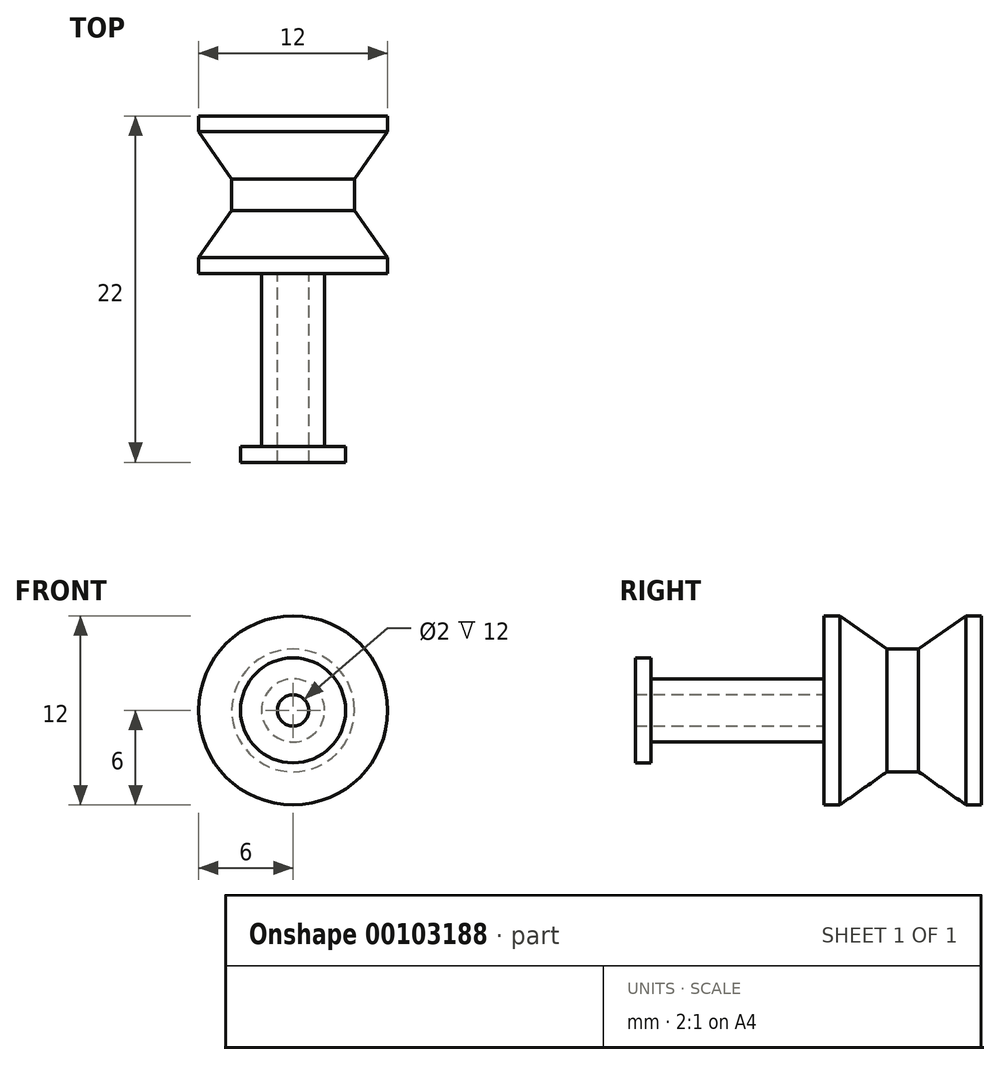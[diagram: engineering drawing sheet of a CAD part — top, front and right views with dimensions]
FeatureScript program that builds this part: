
annotation { "Feature Type Name" : "Feature", "Feature Type Description" : "" }
export const myFeature = defineFeature(function(context is Context, id is Id, definition is map)
    precondition{}
    {
        {
            var Q0;
            Q0=qCreatedBy(makeId("Front.planeOp"),FACE);
            var sketch = newSketch(context, id + "F0", { "sketchPlane" : qUnion([Q0])});
            skCircle(sketch, "E0", {"center": v(0, 0) * mm, "radius": 1 * mm});
            skCircle(sketch, "E1", {"center": v(0, 0) * mm, "radius": 2 * mm});
            skCircle(sketch, "E2", {"center": v(0, 0) * mm, "radius": 3.5 * mm});
            skCircle(sketch, "E3", {"center": v(0, 0) * mm, "radius": 6 * mm});
            skSolve(sketch);
        }
        {
            var Q0;
            Q0=makeQuery(id+"F0.imprint","IMPRINT",FACE,{"disambiguationData":[TD([[makeQuery(id+"F0.imprint","IMPRINT",EDGE,{"derivedFrom":sQuery(id+"F0.wireOp",EDGE,"E0")}),-1.0]])]});
            extrude(context, id + "F1", {"entities" : qUnion([Q0]), "depth" : 22 * mm});
        }
        {
            var Q0;
            Q0=makeQuery(id+"F0.imprint","IMPRINT",FACE,{"disambiguationData":[TD([[makeQuery(id+"F0.imprint","IMPRINT",EDGE,{"derivedFrom":sQuery(id+"F0.wireOp",EDGE,"E2")}),-1.0]])]});
            var Q1;
            Q1=makeQuery(id+"F0.imprint","IMPRINT",FACE,{"disambiguationData":[TD([[makeQuery(id+"F0.imprint","IMPRINT",EDGE,{"derivedFrom":sQuery(id+"F0.wireOp",EDGE,"E1")}),-1.0]])]});
            var Q2;
            Q2=makeQuery(id+"F0.imprint","IMPRINT",FACE,{"disambiguationData":[TD([[makeQuery(id+"F0.imprint","IMPRINT",EDGE,{"derivedFrom":sQuery(id+"F0.wireOp",EDGE,"E0")}),-1.0]])]});
            var Q3;
            Q3=makeQuery(id+"F0.imprint","IMPRINT",FACE,{"disambiguationData":[TD([[makeQuery(id+"F0.imprint","IMPRINT",EDGE,{"derivedFrom":sQuery(id+"F0.wireOp",EDGE,"E0")}),1.0]])]});
            extrude(context, id + "F2", {"entities" : qUnion([Q0, Q1, Q2, Q3]), "depth" : 1 * mm});
        }
        {
            var Q0;
            Q0=makeQuery(id+"F2.opExtrude","CAP_FACE",FACE,{"disambiguationData":[OSD([sQuery(id+"F0.wireOp",EDGE,"E3")])],"isStart":false});
            extrude(context, id + "F3", {"entities" : qUnion([Q0]), "operationType" : NewBodyOperationType.ADD, "depth" : 3 * mm, "hasDraft" : true, "draftAngle" : 35 * degree, "draftPullDirection" : true});
        }
        {
            var Q0;
            Q0=makeQuery(id+"F3.opExtrude","CAP_FACE",FACE,{"disambiguationData":[OSD([sQuery(id+"F0.wireOp",EDGE,"E3")])],"isStart":false});
            extrude(context, id + "F4", {"entities" : qUnion([Q0]), "operationType" : NewBodyOperationType.ADD, "depth" : 2 * mm});
        }
        {
            var Q0;
            Q0=makeQuery(id+"F4.opExtrude","CAP_FACE",FACE,{"disambiguationData":[OSD([sQuery(id+"F0.wireOp",EDGE,"E3")])],"isStart":false});
            extrude(context, id + "F5", {"entities" : qUnion([Q0]), "operationType" : NewBodyOperationType.ADD, "depth" : 3 * mm, "hasDraft" : true, "draftAngle" : 35 * degree});
        }
        {
            var Q0;
            Q0=makeQuery(id+"F5.opExtrude","CAP_FACE",FACE,{"disambiguationData":[OSD([sQuery(id+"F0.wireOp",EDGE,"E3")])],"isStart":false});
            extrude(context, id + "F6", {"entities" : qUnion([Q0]), "operationType" : NewBodyOperationType.ADD, "depth" : 1 * mm});
        }
        {
            var Q0;
            Q0=makeQuery(id+"F1.opExtrude","CAP_FACE",FACE,{"disambiguationData":[OSD([sQuery(id+"F0.wireOp",EDGE,"E0"),sQuery(id+"F0.wireOp",EDGE,"E1")])],"isStart":false});
            var sketch = newSketch(context, id + "F7", { "sketchPlane" : qUnion([Q0])});
            skCircle(sketch, "E4", {"center": v(0, 0) * mm, "radius": 3.34 * mm});
            skSolve(sketch);
        }
        {
            var Q0;
            Q0=makeQuery(id+"F7.imprint","IMPRINT",FACE,{"disambiguationData":[TD([[makeQuery(id+"F7.imprint","IMPRINT",EDGE,{"derivedFrom":makeQuery(id+"F1.opExtrude","CAP_EDGE",EDGE,{"disambiguationData":[OSD([sQuery(id+"F0.wireOp",EDGE,"E0")])],"isStart":false})}),-1.0]])]});
            var Q1;
            Q1=makeQuery(id+"F7.imprint","IMPRINT",FACE,{"disambiguationData":[TD([[makeQuery(id+"F7.imprint","IMPRINT",EDGE,{"derivedFrom":sQuery(id+"F7.wireOp",EDGE,"E4")}),1.0]])]});
            extrude(context, id + "F8", {"entities" : qUnion([Q0, Q1]), "operationType" : NewBodyOperationType.ADD, "oppositeDirection" : true, "depth" : 1 * mm});
        }
    });
